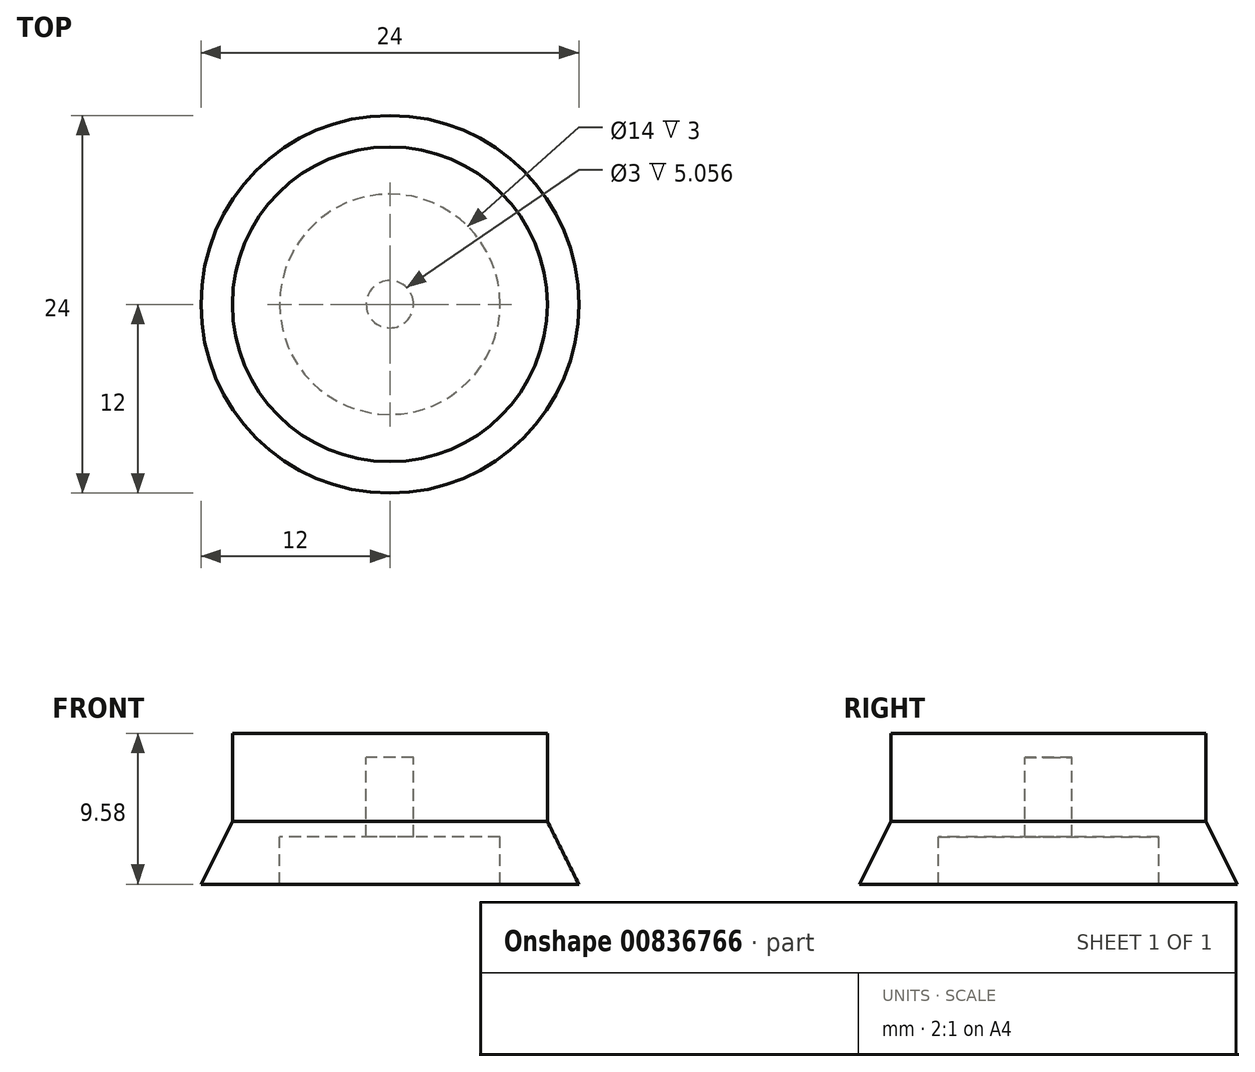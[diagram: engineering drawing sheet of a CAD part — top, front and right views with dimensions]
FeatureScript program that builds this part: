
annotation { "Feature Type Name" : "Feature", "Feature Type Description" : "" }
export const myFeature = defineFeature(function(context is Context, id is Id, definition is map)
    precondition{}
    {
        {
            var Q0;
            Q0=qCreatedBy(makeId("Front.planeOp"),FACE);
            var sketch = newSketch(context, id + "F0", { "sketchPlane" : qUnion([Q0])});
            skLineSegment(sketch, "E0", {"start": v(0, 23.2) * mm, "end": v(0, -18.54) * mm, "construction": true});
            skLineSegment(sketch, "E1.bottom", {"start": v(-10, 9.58) * mm, "end": v(0, 9.58) * mm});
            skLineSegment(sketch, "E1.top", {"start": v(-10, 0) * mm, "end": v(-7, 0) * mm});
            skLineSegment(sketch, "E1.left", {"start": v(-10, 9.58) * mm, "end": v(-10, 4) * mm});
            skLineSegment(sketch, "E1.right", {"start": v(0, 9.58) * mm, "end": v(0, 0) * mm});
            skPoint(sketch, "E2.endSnap0", {"position": v(-5, 0) * mm});
            skLineSegment(sketch, "E3", {"start": v(-12, 0) * mm, "end": v(-10, 0) * mm});
            skPoint(sketch, "E4.newPointA", {"position": v(-10, -5.42) * mm});
            skPoint(sketch, "E4.newPointB", {"position": v(-10, 2.08) * mm});
            skLineSegment(sketch, "E5", {"start": v(-12, 0) * mm, "end": v(-10, 4) * mm});
            skLineSegment(sketch, "E6.top", {"start": v(0, 8.06) * mm, "end": v(-1.5, 8.06) * mm});
            skLineSegment(sketch, "E6.left", {"start": v(0, 0) * mm, "end": v(0, 8.06) * mm});
            skLineSegment(sketch, "E6.right", {"start": v(-1.5, 3) * mm, "end": v(-1.5, 8.06) * mm});
            skLineSegment(sketch, "E7.bottom", {"start": v(-1.5, 3) * mm, "end": v(-7, 3) * mm});
            skLineSegment(sketch, "E7.right", {"start": v(-7, 3) * mm, "end": v(-7, 0) * mm});
            skPoint(sketch, "E8.trimOffspring.end.orphan", {"position": v(-1.5, 0) * mm});
            skSolve(sketch);
        }
        {
            var Q0;
            Q0 = qSketchRegion(id + "F0", true);
            var Q1;
            Q1=sQuery(id+"F0.wireOp",EDGE,"E1.right");
            revolve(context, id + "F1", {"surfaceOperationType" : NewSurfaceOperationType.NEW, "entities" : qUnion([Q0]), "axis" : qUnion([Q1]), "revolveType" : RevolveType.FULL});
        }
    });
